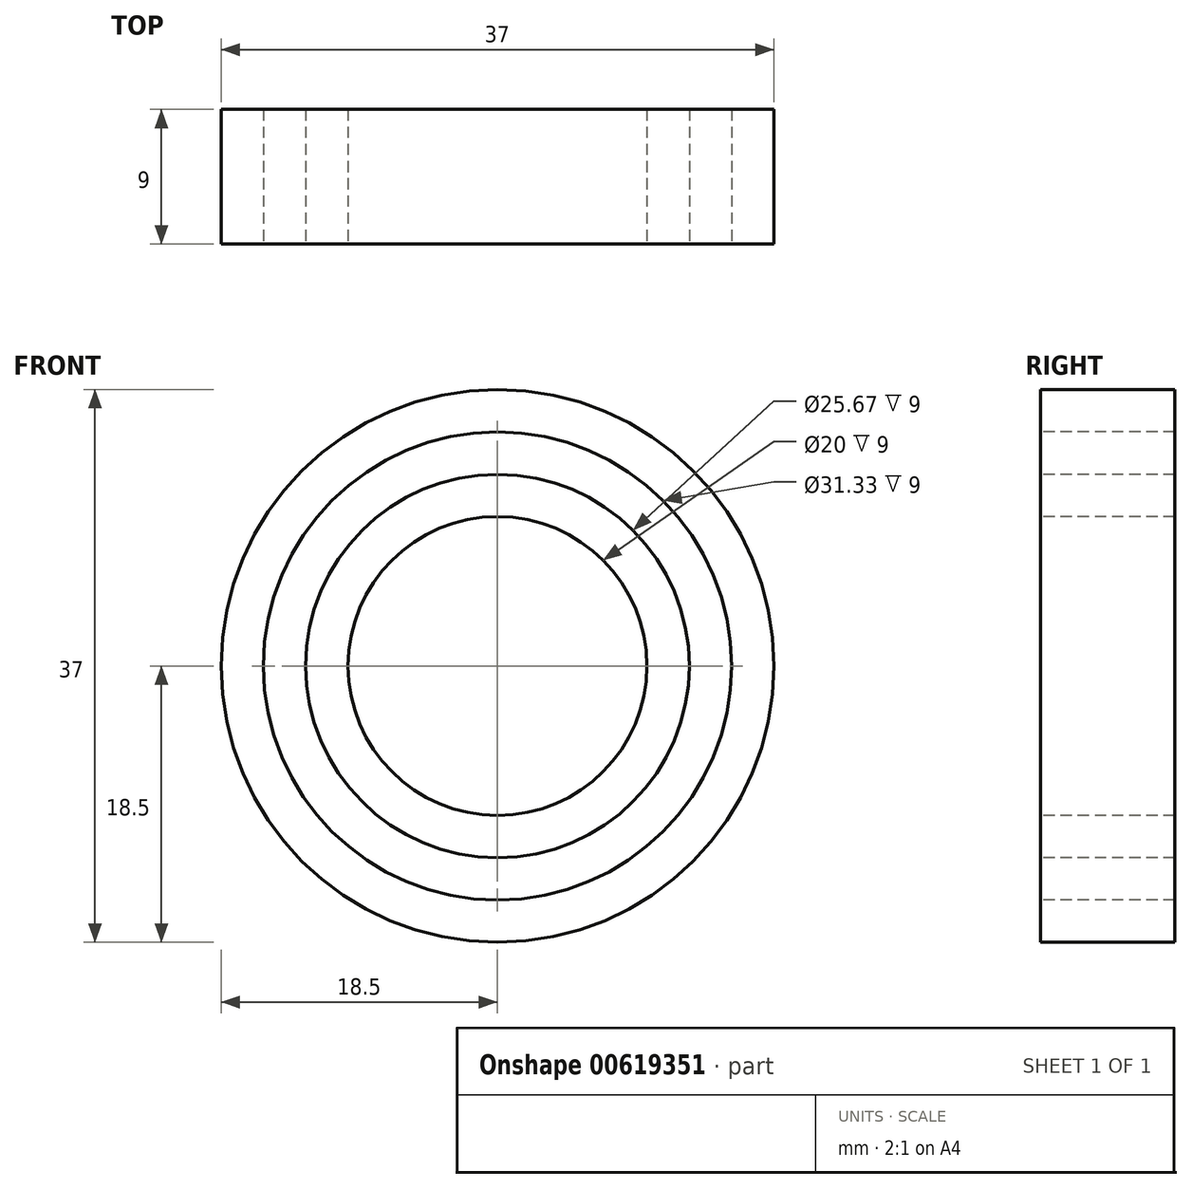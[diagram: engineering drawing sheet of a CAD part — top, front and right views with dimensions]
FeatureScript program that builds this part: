
annotation { "Feature Type Name" : "Feature", "Feature Type Description" : "" }
export const myFeature = defineFeature(function(context is Context, id is Id, definition is map)
    precondition{}
    {
        {
            var Q0;
            Q0=qCreatedBy(makeId("Top.planeOp"),FACE);
            var sketch = newSketch(context, id + "F0", { "sketchPlane" : qUnion([Q0])});
            skLineSegment(sketch, "E0", {"start": v(0, 0) * mm, "end": v(0, 9) * mm});
            skLineSegment(sketch, "E1", {"start": v(0, 9) * mm, "end": v(2.83, 9) * mm});
            skLineSegment(sketch, "E2", {"start": v(5.67, 9) * mm, "end": v(8.5, 9) * mm});
            skLineSegment(sketch, "E3", {"start": v(8.5, 9) * mm, "end": v(8.5, 0) * mm});
            skLineSegment(sketch, "E4", {"start": v(8.5, 0) * mm, "end": v(5.67, 0) * mm});
            skLineSegment(sketch, "E5", {"start": v(5.67, 0) * mm, "end": v(5.67, 9) * mm});
            skLineSegment(sketch, "E6", {"start": v(2.83, 9) * mm, "end": v(2.83, 0) * mm});
            skLineSegment(sketch, "E7", {"start": v(2.83, 0) * mm, "end": v(0, 0) * mm});
            skLineSegment(sketch, "E8", {"start": v(18.5, 0) * mm, "end": v(18.5, 9) * mm, "construction": true});
            skLineSegment(sketch, "E9", {"start": v(2.83, 9) * mm, "end": v(5.67, 9) * mm});
            skLineSegment(sketch, "E10", {"start": v(2.83, 0) * mm, "end": v(5.67, 0) * mm});
            skSolve(sketch);
        }
        {
            var Q0;
            Q0=makeQuery(id+"F0.imprint","IMPRINT",FACE,{"disambiguationData":[TD([[makeQuery(id+"F0.imprint","IMPRINT",EDGE,{"derivedFrom":sQuery(id+"F0.wireOp",EDGE,"E0")}),-1.0]])]});
            var Q1;
            Q1=sQuery(id+"F0.wireOp",EDGE,"E8");
            revolve(context, id + "F1", {"entities" : qUnion([Q0]), "axis" : qUnion([Q1]), "revolveType" : RevolveType.FULL});
        }
        {
            var Q0;
            Q0=makeQuery(id+"F0.imprint","IMPRINT",FACE,{"disambiguationData":[TD([[makeQuery(id+"F0.imprint","IMPRINT",EDGE,{"derivedFrom":sQuery(id+"F0.wireOp",EDGE,"E5")}),1.0]])]});
            var Q1;
            Q1=sQuery(id+"F0.wireOp",EDGE,"E8");
            revolve(context, id + "F2", {"entities" : qUnion([Q0]), "axis" : qUnion([Q1]), "revolveType" : RevolveType.FULL});
        }
        {
            var Q0;
            Q0=makeQuery(id+"F0.imprint","IMPRINT",FACE,{"disambiguationData":[TD([[makeQuery(id+"F0.imprint","IMPRINT",EDGE,{"derivedFrom":sQuery(id+"F0.wireOp",EDGE,"E2")}),-1.0]])]});
            var Q1;
            Q1=sQuery(id+"F0.wireOp",EDGE,"E8");
            revolve(context, id + "F3", {"entities" : qUnion([Q0]), "axis" : qUnion([Q1]), "revolveType" : RevolveType.FULL});
        }
    });
